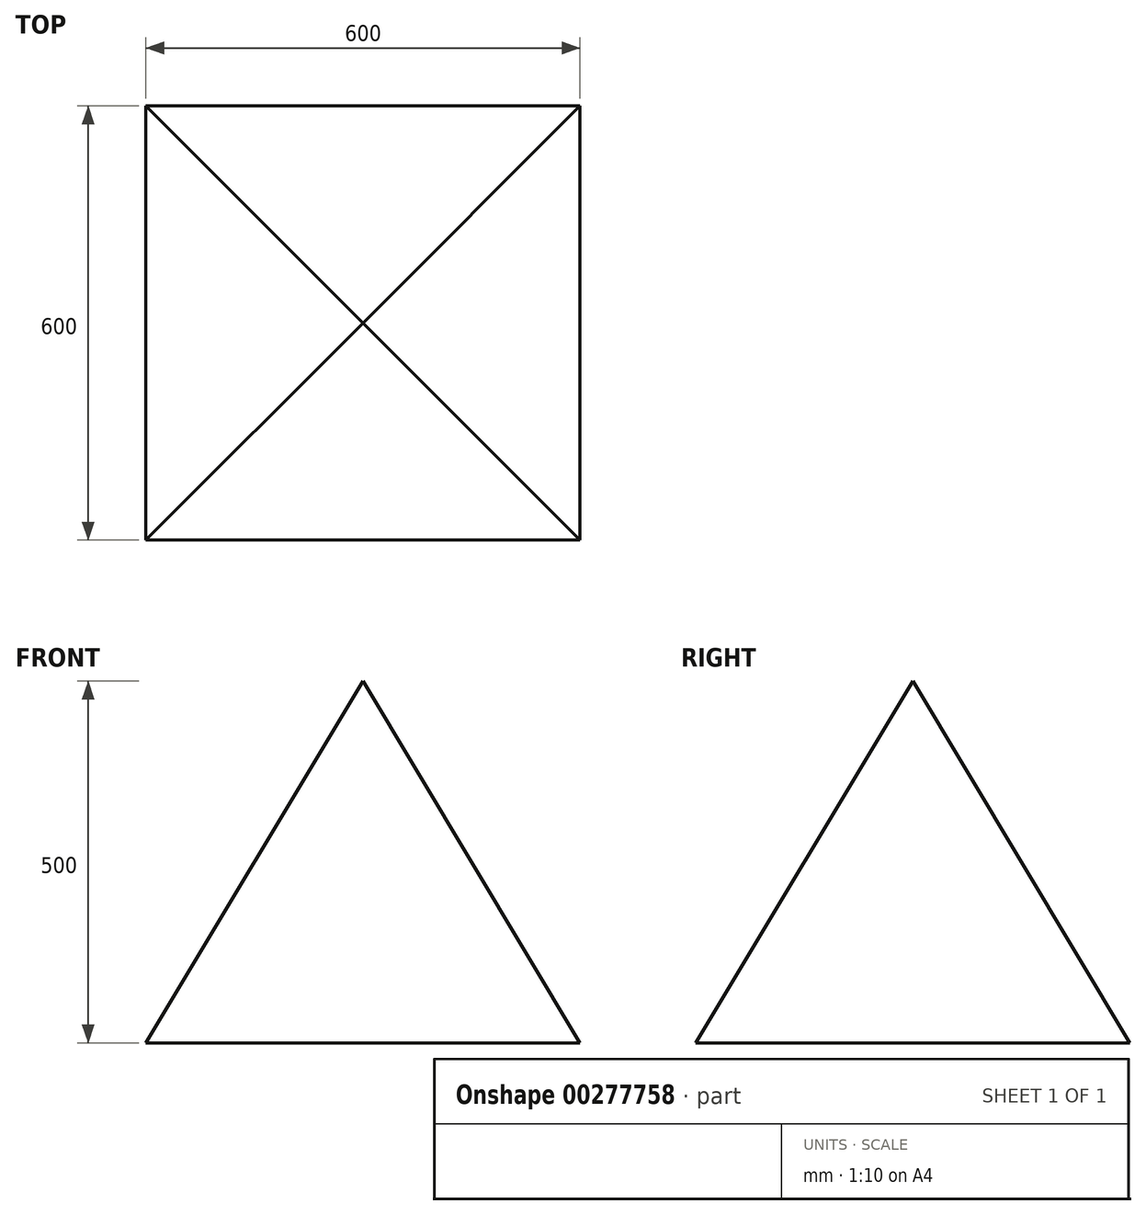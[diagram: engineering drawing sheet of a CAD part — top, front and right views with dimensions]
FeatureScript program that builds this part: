
annotation { "Feature Type Name" : "Feature", "Feature Type Description" : "" }
export const myFeature = defineFeature(function(context is Context, id is Id, definition is map)
    precondition{}
    {
        {
            var Q0;
            Q0=qCreatedBy(makeId("Top.planeOp"),FACE);
            var sketch = newSketch(context, id + "F0", { "sketchPlane" : qUnion([Q0])});
            skLineSegment(sketch, "E0.bottom", {"start": v(300, 300) * mm, "end": v(-300, 300) * mm});
            skLineSegment(sketch, "E0.top", {"start": v(300, -300) * mm, "end": v(-300, -300) * mm});
            skLineSegment(sketch, "E0.left", {"start": v(300, 300) * mm, "end": v(300, -300) * mm});
            skLineSegment(sketch, "E0.right", {"start": v(-300, 300) * mm, "end": v(-300, -300) * mm});
            skPoint(sketch, "E0.middle", {"position": v(0, 0) * mm});
            skSolve(sketch);
        }
        {
            var Q0;
            Q0=qCreatedBy(makeId("Top.planeOp"),FACE);
            cPlane(context, id + "F1", {"entities" : qUnion([Q0]), "cplaneType" : CPlaneType.OFFSET, "offset" : 500 * mm, "width" : 150 * mm, "height" : 150 * mm});
        }
        {
            var Q0;
            Q0=qCreatedBy(id+"F1.planeOp",FACE);
            var sketch = newSketch(context, id + "F2", { "sketchPlane" : qUnion([Q0])});
            skPoint(sketch, "E1", {"position": v(0, 0) * mm});
            skSolve(sketch);
        }
        {
            var Q0;
            Q0=sQuery(id+"F2.wireOp",VERTEX,"E1");
            var Q1;
            Q1=makeQuery(id+"F0.imprint","IMPRINT",FACE,{"disambiguationData":[TD([[makeQuery(id+"F0.imprint","IMPRINT",EDGE,{"derivedFrom":sQuery(id+"F0.wireOp",EDGE,"E0.bottom")}),1.0]])]});
            var Q2;
            Q2=sQuery(id+"F2.wireOp",VERTEX,"E1");
            var Q3;
            Q3=makeQuery(id+"F0.imprint","IMPRINT",FACE,{"disambiguationData":[TD([[makeQuery(id+"F0.imprint","IMPRINT",EDGE,{"derivedFrom":sQuery(id+"F0.wireOp",EDGE,"E0.bottom")}),1.0]])]});
            loft(context, id + "F3", {"bodyType" : ToolBodyType.SURFACE, "operationType" : NewBodyOperationType.ADD, "sheetProfilesArray" : [{ "sheetProfileEntities" : qUnion([Q0]) }, { "sheetProfileEntities" : qUnion([Q1]) }], "wireProfilesArray" : [{ "wireProfileEntities" : qUnion([Q2]) }, { "wireProfileEntities" : qUnion([Q3]) }]});
        }
    });
